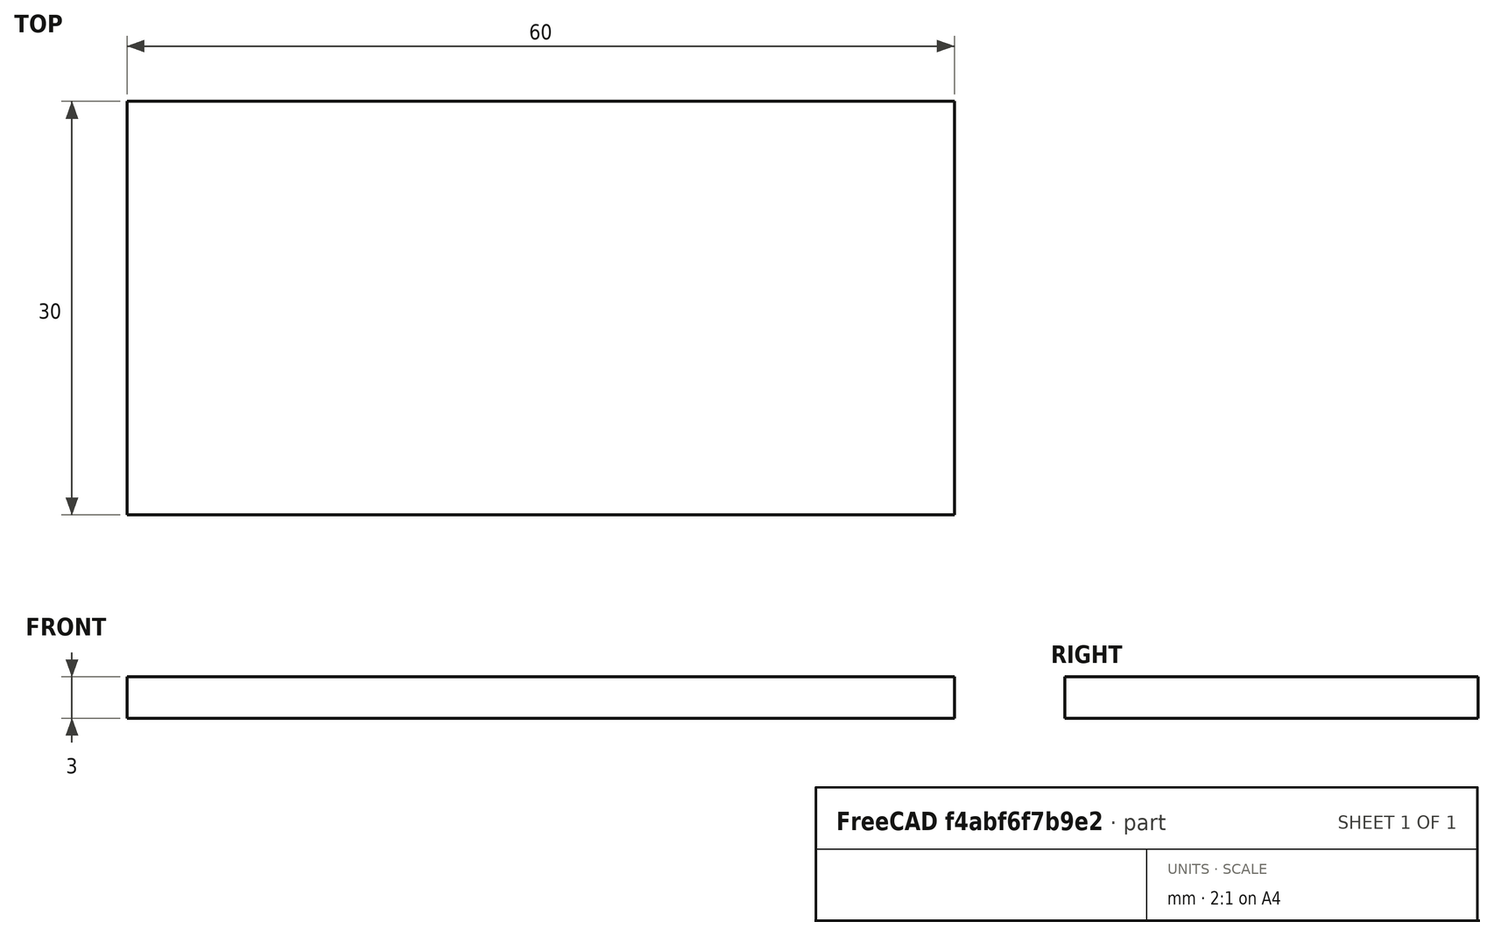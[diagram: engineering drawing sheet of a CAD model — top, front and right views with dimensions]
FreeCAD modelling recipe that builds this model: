
FCSTD DOCUMENT  (FreeCAD 0.17R13217 (Git))
Label: 09-mesa
License: All rights reserved
LicenseURL: http://en.wikipedia.org/wiki/All_rights_reserved
objects: Sketcher::SketchObject×1, PartDesign::Pad×1, PartDesign::Plane×1, PartDesign::Body×1
note: 5 computed .brp shape members not serialized (recipe doc carries the construction recipe); baked Part::Feature solids carry a one-line shape summary decoded from their .brp

FEATURE [Sketcher::SketchObject] Sketch
  MapMode = 5
  Support = -> [XY_Plane]
  sketch-geometry (4):
    g0: LineSegment StartX=-30 StartY=15 StartZ=0 EndX=30 EndY=15 EndZ=0
    g1: LineSegment StartX=30 StartY=15 StartZ=0 EndX=30 EndY=-15 EndZ=0
    g2: LineSegment StartX=30 StartY=-15 StartZ=0 EndX=-30 EndY=-15 EndZ=0
    g3: LineSegment StartX=-30 StartY=-15 StartZ=0 EndX=-30 EndY=15 EndZ=0
  constraints (11):
    c: Coincident(g0,g1)
    c: Coincident(g1,g2)
    c: Coincident(g2,g3)
    c: Coincident(g3,g0)
    c: Horizontal(g0)
    c: Horizontal(g2)
    c: Vertical(g1)
    c: Vertical(g3)
    c: Symmetric(g0,g1,g-1)
    c: DistanceX(g0,g0) = 60
    c: DistanceY(g3,g3) = 30
FEATURE [PartDesign::Pad] Pad
  Length = 3
  Length2 = 100
  Profile = -> Sketch
  Refine = true
  Type = 0
FEATURE [PartDesign::Plane] DatumPlane
  MapMode = 5
  Placement = pos=(0,0,0) rot=(1,0,0;3.14159rad)
  Support = -> [Pad]
FEATURE [PartDesign::Body] Body
  Group = -> [Sketch,Pad,DatumPlane]
  Origin = -> Origin
  Tip = -> Pad
